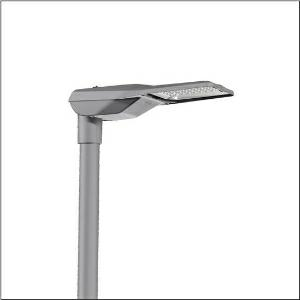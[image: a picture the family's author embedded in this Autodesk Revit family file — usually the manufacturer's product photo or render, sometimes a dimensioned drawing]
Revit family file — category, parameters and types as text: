
# Revit family: streetlight_sl_21_mini___st0_8a_5xe2c33s08gb_9548
name_source: partatom
category: Lighting Fixtures
units: mm (PartAtom-declared; Revit-internal decimal feet)

## family parameters
Cut with Voids When Loaded = No
Host = Face
Light Source = No
Part Type = Normal
Room Calculation Point = No
Round Connector Dimension = Use Diameter
Shared = No

## types (1)
- --- (1 x LED, 5940 lm, 40.4 W, 3000K)
    Apparent Load = 40 VA
    CIE Flux Codes = 38 75 97 100 100
    Color Rendering = 70
    Color Temperature = 3000K
    Default Elevation = 1800 mm
    Description = Streetlight SL 21 mini, mast luminaire, primary light control with lens, of PMMA, primary optical cover: cover, of toughened safety glass, transparent, light distribution: ST0.8a, light emission: direct distribution, primary light characteristic: asymmetric, installation type: side-entry, post-top, LED, High Power LED, rated luminous flux: 5.940lm, luminous efficacy: 147lm/W, light colour: 730, colour temperature: 3000K, control gear: D4i, control: overheat protection, constant luminous flux control, time-dependent luminous flux control, flexible luminous flux parameterisation, pre-setting: logarithmic dimming characteristic, mains connection: 220..240V, AC, 50/60Hz, start of lifetime: 40W, end of service life: 41W, reduction: 19W, luminaire housing, of diecast aluminium, powder-coated, SITECO metallic grey (DB 702S), corrosivity category C5 high according to DIN EN ISO 12944, please order mast flange separately, inclination adjustable: 0°, 5°, 10°, 15°, sealing non-destructively replaceable, multi-level sealing system, length: 628mm, width: 235mm, height: 110mm, mast flange for spigot size: 42mm (side-entry): 5XC10008XM4, 60/48mm (side-entry/post-top): 5XC10108XM2, 76/60mm (side-entry/post-top): 5XC10108XM1, mounting height: 4..8m, Smart Interface above, protection rating (complete): IP66, insulation class (complete): insulation class II (safety insulation), certification: CE, ENEC, ENEC+, VDE, impact resistance: IK10, permissible operating ambient temperature for outdoor applications: -40..+50°C, standard-compliant lighting for roads and squares, packaging unit: 1 piece

Light Distribution: ST0.8a
    Height = 110 mm
    Lamp = 1 x LED
    Lamp Light Flux = 5940 lm
    Lamp Power = 40.4 W
    Lamp count = 1
    Length = 625 mm
    Luminous efficacy = 147 lm/W
    Manufacturer = Siteco
    ModVariant = No
    Model = 5XE2C33S08GB
    Number of Poles = 1
    OnlyDefault = Yes
    Power Factor = 1
    Product Name = Streetlight SL 21 mini | ST0.8a
    Product group = mast luminaire | pylon top
    ProductGroupID = 6100
    Protection Class = Protection class II
    Protection Degree = IP 66
    RLX_Detail_Level = 1
    RLX_Emergency_Light_Flux = 0 lm
    RLX_Emergency_Type = 0
    RLX_Emergency_Type_DB = No
    RlxData = <blob elided: 26229 chars, md5=6dafd8a1>
    Socket = socket
    Standby Power = 0 W
    System Light Flux = 5940 lm
    System Power = 40 W
    Type Comments = factory setting: luminous flux: 100 % | dim-lin: 254 | 812 mA
    Type Image = l_1003515.jpg
    URL = http://relux.com
    VarID = @adj_183029
    Voltage = 0 V
    Weight = 0.00 kg
    Width = 234 mm

## geometry (parser evidence)
native form markers: Blend x4, Sweep x11
no freeform markers — native parametric forms only
